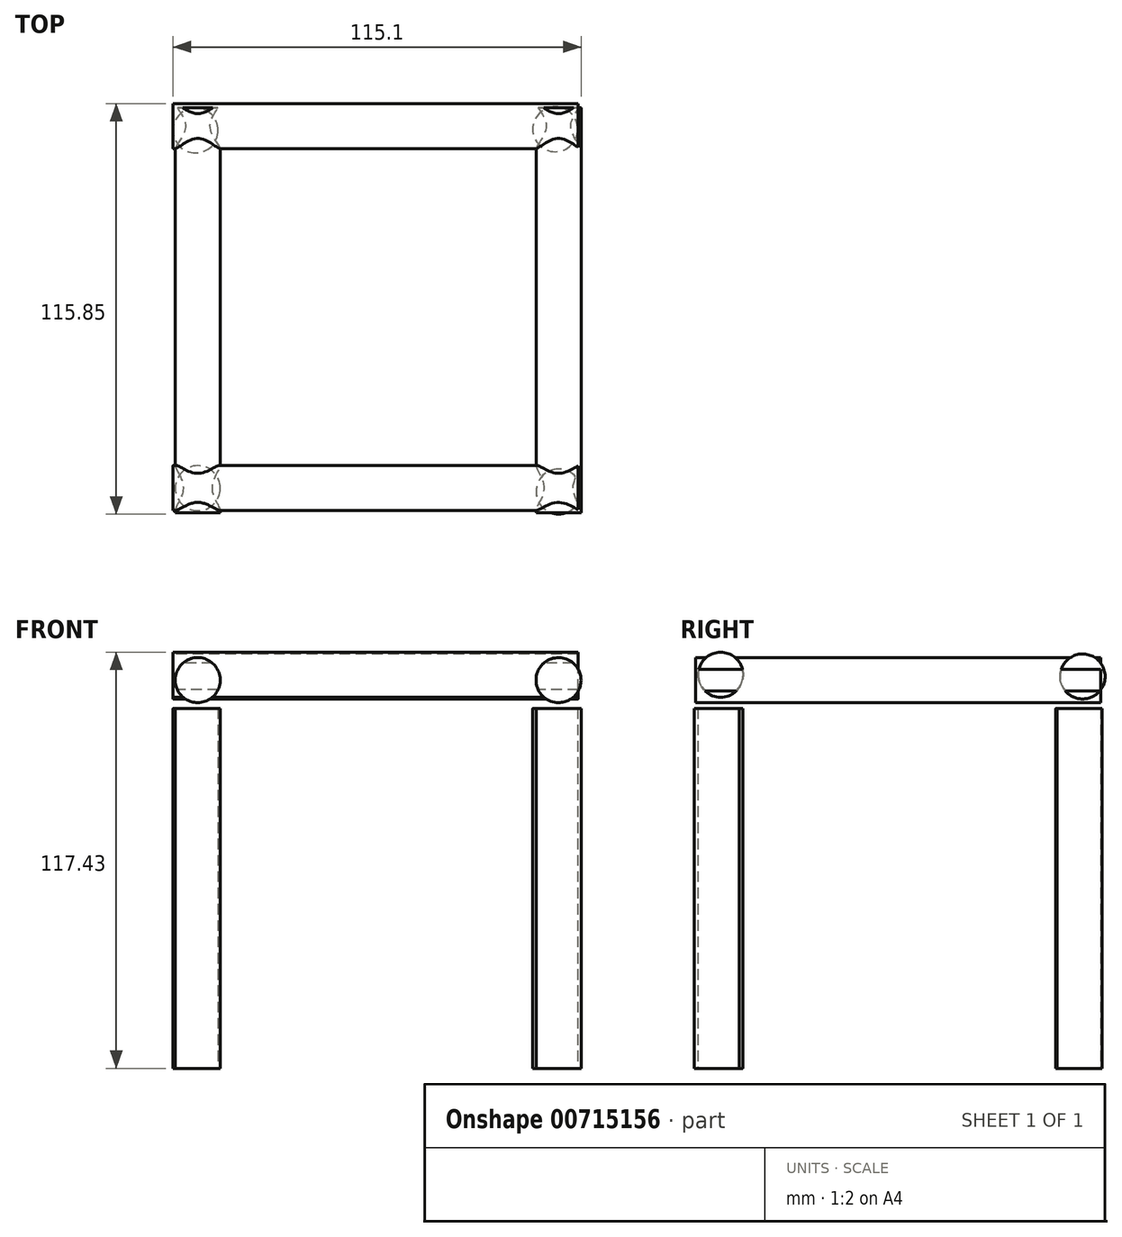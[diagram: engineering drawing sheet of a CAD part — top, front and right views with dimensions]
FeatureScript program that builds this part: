
annotation { "Feature Type Name" : "Feature", "Feature Type Description" : "" }
export const myFeature = defineFeature(function(context is Context, id is Id, definition is map)
    precondition{}
    {
        {
            var Q0;
            Q0=qCreatedBy(makeId("Top.planeOp"),FACE);
            var sketch = newSketch(context, id + "F0", { "sketchPlane" : qUnion([Q0])});
            skPoint(sketch, "E0.middle", {"position": v(0, 0) * mm});
            skCircle(sketch, "E1", {"center": v(-50.8, 50.8) * mm, "radius": 6.35 * mm});
            skCircle(sketch, "E2", {"center": v(50.66, 51.13) * mm, "radius": 6.35 * mm});
            skCircle(sketch, "E3", {"center": v(51.6, -51.13) * mm, "radius": 6.35 * mm});
            skCircle(sketch, "E4", {"center": v(-50.19, -50.19) * mm, "radius": 6.35 * mm});
            skSolve(sketch);
        }
        {
            var Q0;
            Q0=makeQuery(id+"F0.imprint","IMPRINT",FACE,{"disambiguationData":[TD([[makeQuery(id+"F0.imprint","IMPRINT",EDGE,{"derivedFrom":sQuery(id+"F0.wireOp",EDGE,"E3")}),1.0]])]});
            var Q1;
            Q1=makeQuery(id+"F0.imprint","IMPRINT",FACE,{"disambiguationData":[TD([[makeQuery(id+"F0.imprint","IMPRINT",EDGE,{"derivedFrom":sQuery(id+"F0.wireOp",EDGE,"E4")}),1.0]])]});
            var Q2;
            Q2=makeQuery(id+"F0.imprint","IMPRINT",FACE,{"disambiguationData":[TD([[makeQuery(id+"F0.imprint","IMPRINT",EDGE,{"derivedFrom":sQuery(id+"F0.wireOp",EDGE,"E1")}),1.0]])]});
            var Q3;
            Q3=makeQuery(id+"F0.imprint","IMPRINT",FACE,{"disambiguationData":[TD([[makeQuery(id+"F0.imprint","IMPRINT",EDGE,{"derivedFrom":sQuery(id+"F0.wireOp",EDGE,"E2")}),1.0]])]});
            extrude(context, id + "F1", {"entities" : qUnion([Q0, Q1, Q2, Q3]), "depth" : 101.6 * mm, "offsetDistance" : 25.4 * mm});
        }
        {
            var Q0;
            Q0=qCreatedBy(makeId("Front.planeOp"),FACE);
            var sketch = newSketch(context, id + "F2", { "sketchPlane" : qUnion([Q0])});
            skCircle(sketch, "E5", {"center": v(51.6, 109.57) * mm, "radius": 6.35 * mm});
            skCircle(sketch, "E6", {"center": v(-50.19, 109.57) * mm, "radius": 6.35 * mm});
            skSolve(sketch);
        }
        {
            var Q0;
            Q0=makeQuery(id+"F2.imprint","IMPRINT",FACE,{"disambiguationData":[TD([[makeQuery(id+"F2.imprint","IMPRINT",EDGE,{"derivedFrom":sQuery(id+"F2.wireOp",EDGE,"E6")}),1.0]])]});
            var Q1;
            Q1=makeQuery(id+"F2.imprint","IMPRINT",FACE,{"disambiguationData":[TD([[makeQuery(id+"F2.imprint","IMPRINT",EDGE,{"derivedFrom":sQuery(id+"F2.wireOp",EDGE,"E5")}),1.0]])]});
            extrude(context, id + "F3", {"entities" : qUnion([Q0, Q1]), "endBound" : BoundingType.SYMMETRIC, "depth" : 114.3 * mm, "offsetDistance" : 25.4 * mm});
        }
        {
            var Q0;
            Q0=qCreatedBy(makeId("Right.planeOp"),FACE);
            var sketch = newSketch(context, id + "F4", { "sketchPlane" : qUnion([Q0])});
            skCircle(sketch, "E7", {"center": v(52.02, 110.6) * mm, "radius": 6.35 * mm});
            skCircle(sketch, "E8", {"center": v(-50.08, 111.08) * mm, "radius": 6.35 * mm});
            skSolve(sketch);
        }
        {
            var Q0;
            Q0 = qSketchRegion(id + "F4", true);
            extrude(context, id + "F5", {"entities" : qUnion([Q0]), "operationType" : NewBodyOperationType.ADD, "endBound" : BoundingType.SYMMETRIC, "depth" : 114.3 * mm, "offsetDistance" : 25.4 * mm});
        }
    });
